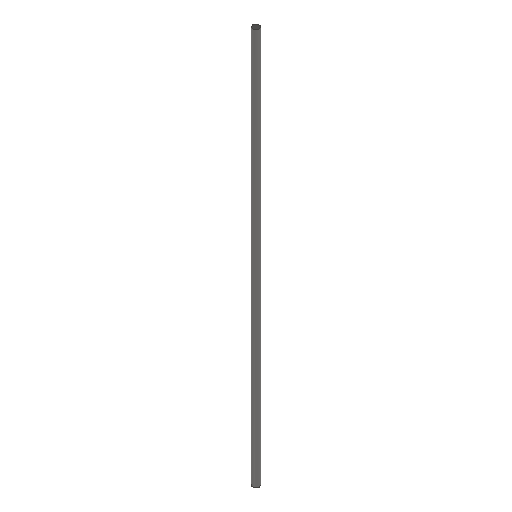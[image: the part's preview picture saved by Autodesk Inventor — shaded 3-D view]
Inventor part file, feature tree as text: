
AUTODESK INVENTOR PART (.ipt)
format: ipt  version: 2021 (Build 250183000, 183)  size: 72,192 bytes
history: native  units: mm
features: extrude x1, sketch x1
ambient origin geometry x8: Origin, YZ Plane, XZ Plane, XY Plane, X Axis, Y Axis, Z Axis, Center Point
bodies: Solid1 (feature_tree)
feature tree (2):
  extrude  "Extrusion1"  Depth=1160.0mm TaperAngle=0.0deg
  sketch  "Sketch1"  dims[d0=20.0mm d1=1160.0mm d2=0.0mm]
